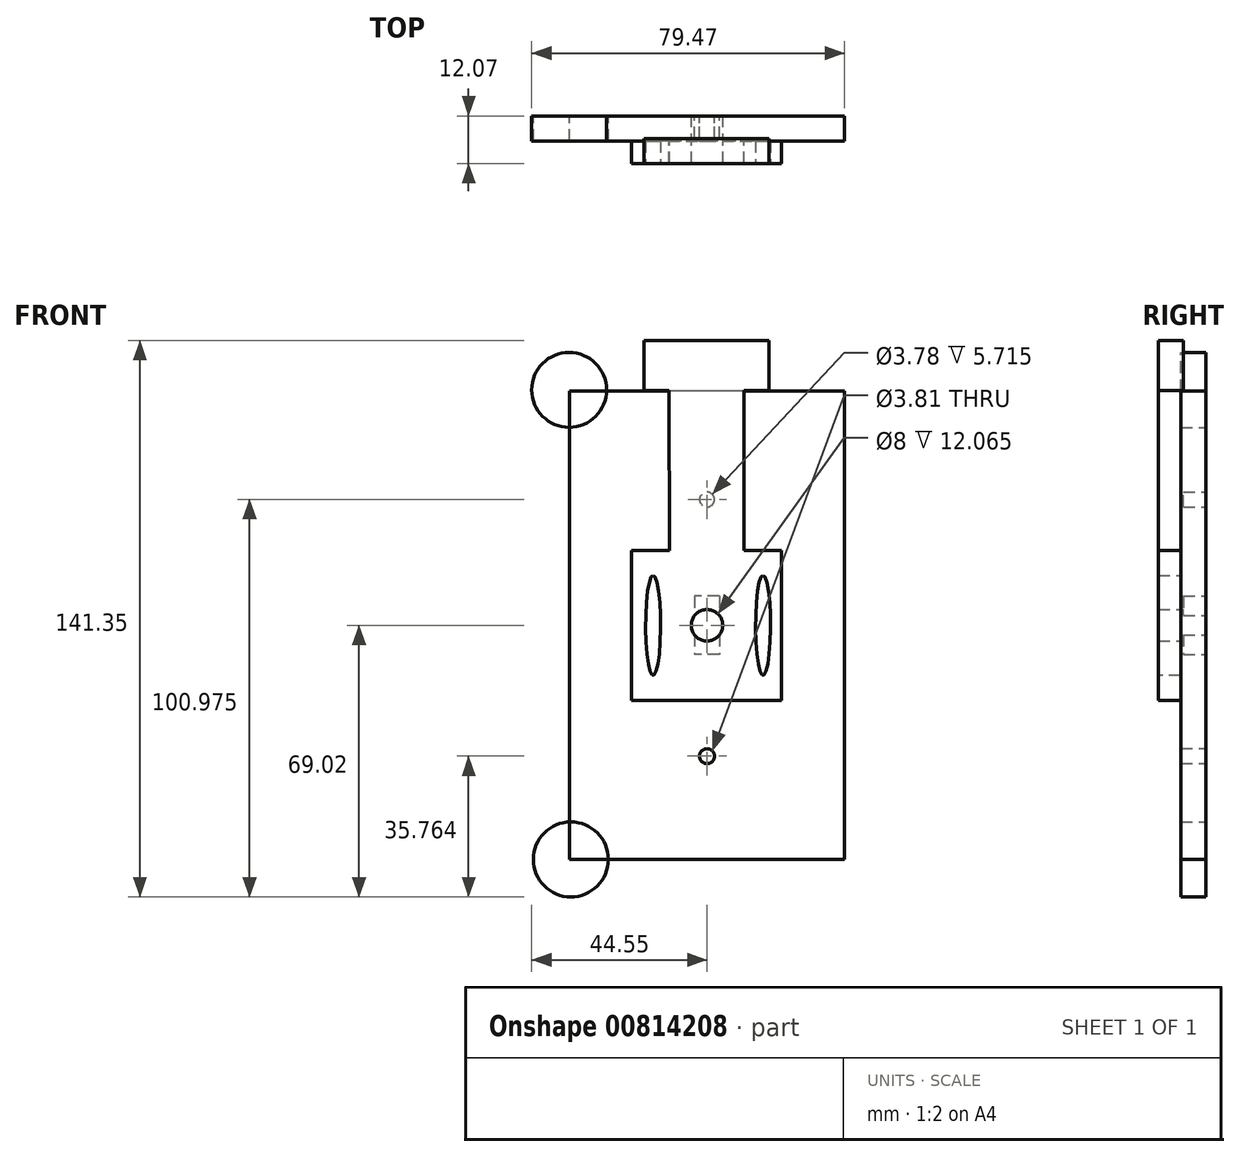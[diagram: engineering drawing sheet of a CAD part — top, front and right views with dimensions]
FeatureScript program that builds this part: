
annotation { "Feature Type Name" : "Feature", "Feature Type Description" : "" }
export const myFeature = defineFeature(function(context is Context, id is Id, definition is map)
    precondition{}
    {
        {
            var Q0;
            Q0=qCreatedBy(makeId("Front.planeOp"),FACE);
            var sketch = newSketch(context, id + "F0", { "sketchPlane" : qUnion([Q0])});
            skLineSegment(sketch, "E0.bottom", {"start": v(34.93, 59.53) * mm, "end": v(-34.93, 59.53) * mm});
            skLineSegment(sketch, "E0.top", {"start": v(34.92, -59.53) * mm, "end": v(-34.93, -59.53) * mm});
            skLineSegment(sketch, "E0.left", {"start": v(34.93, 59.53) * mm, "end": v(34.92, -59.53) * mm});
            skLineSegment(sketch, "E0.right", {"start": v(-34.93, 59.53) * mm, "end": v(-34.93, -59.53) * mm});
            skPoint(sketch, "E0.middle", {"position": v(0, 0) * mm});
            skLineSegment(sketch, "E1.bottom", {"start": v(3.18, 7.4) * mm, "end": v(-3.17, 7.4) * mm});
            skLineSegment(sketch, "E1.top", {"start": v(3.17, -7.4) * mm, "end": v(-3.18, -7.4) * mm});
            skLineSegment(sketch, "E1.left", {"start": v(3.18, 7.4) * mm, "end": v(3.17, -7.4) * mm});
            skLineSegment(sketch, "E1.right", {"start": v(-3.17, 7.4) * mm, "end": v(-3.18, -7.4) * mm});
            skCircle(sketch, "E2", {"center": v(0, 31.96) * mm, "radius": 1.9 * mm});
            skPoint(sketch, "E2.centerSnap0", {"position": v(0, 7.4) * mm});
            skCircle(sketch, "E3", {"center": v(0, -33.26) * mm, "radius": 1.9 * mm});
            skSolve(sketch);
        }
        {
            var Q0;
            Q0=qCreatedBy(makeId("Front.planeOp"),FACE);
            var sketch = newSketch(context, id + "F1", { "sketchPlane" : qUnion([Q0])});
            skCircle(sketch, "E4", {"center": v(-35.02, 59.81) * mm, "radius": 9.53 * mm});
            skSolve(sketch);
        }
        {
            var Q0;
            Q0=qCreatedBy(makeId("Front.planeOp"),FACE);
            var sketch = newSketch(context, id + "F2", { "sketchPlane" : qUnion([Q0])});
            skCircle(sketch, "E5", {"center": v(-34.6, -59.5) * mm, "radius": 9.53 * mm});
            skSolve(sketch);
        }
        {
            var Q0;
            Q0=makeQuery(id+"F2.imprint","IMPRINT",FACE,{"disambiguationData":[TD([[makeQuery(id+"F2.imprint","IMPRINT",EDGE,{"derivedFrom":sQuery(id+"F2.wireOp",EDGE,"E5")}),1.0]])]});
            var Q1;
            Q1=makeQuery(id+"F0.imprint","IMPRINT",FACE,{"disambiguationData":[TD([[makeQuery(id+"F0.imprint","IMPRINT",EDGE,{"derivedFrom":sQuery(id+"F0.wireOp",EDGE,"E0.bottom")}),1.0]])]});
            var Q2;
            Q2=makeQuery(id+"F1.imprint","IMPRINT",FACE,{"disambiguationData":[TD([[makeQuery(id+"F1.imprint","IMPRINT",EDGE,{"derivedFrom":sQuery(id+"F1.wireOp",EDGE,"E4")}),1.0]])]});
            extrude(context, id + "F3", {"entities" : qUnion([Q0, Q1, Q2]), "depth" : 6.35 * mm, "offsetDistance" : 25.4 * mm});
        }
        {
            var Q0;
            Q0=makeQuery(id+"FBm9dElFGxXl51s_0.boolean.opBoolean","MERGE",FACE,{"derivedFrom":[makeQuery(id+"F3.opExtrude","CAP_FACE",FACE,{"disambiguationData":[OSD([sQuery(id+"F0.wireOp",EDGE,"E0.bottom"),sQuery(id+"F0.wireOp",EDGE,"E0.top"),sQuery(id+"F0.wireOp",EDGE,"E0.left"),sQuery(id+"F0.wireOp",EDGE,"E0.right")])],"isStart":false}),makeQuery(id+"FBm9dElFGxXl51s_0.opExtrude","CAP_FACE",FACE,{"disambiguationData":[OSD([sQuery(id+"FwdLjQRzTwuGbji_0.wireOp",EDGE,"bJfUg37Y-0sjC-gCHG-03pR-bU85yGZvt3Yf.left"),sQuery(id+"FwdLjQRzTwuGbji_0.wireOp",EDGE,"bJfUg37Y-0sjC-gCHG-03pR-bU85yGZvt3Yf.right"),sQuery(id+"FwdLjQRzTwuGbji_0.wireOp",EDGE,"DSwXmp3Y-NZgs-XlkP-MrdE-YPkT81guO0ga"),sQuery(id+"FwdLjQRzTwuGbji_0.wireOp",EDGE,"yhkVxWKS-fieb-baY7-XOx3-TyVL69QeHBbo"),sQuery(id+"FwdLjQRzTwuGbji_0.wireOp",EDGE,"tSnspYBW-VqIu-ENpb-q0uR-903lSlMSbRlf"),sQuery(id+"FwdLjQRzTwuGbji_0.wireOp",EDGE,"O0cluCkd-JC2S-dvMv-2QXM-CzPiqj9PooOO"),sQuery(id+"FwdLjQRzTwuGbji_0.wireOp",EDGE,"txsKDkrA-VlTc-3cXs-rglu-60bT2i7TrSKH"),sQuery(id+"FwdLjQRzTwuGbji_0.wireOp",EDGE,"3i0H6R7e-R6fp-PJKQ-zfIY-D4jAGeBqw7su"),sQuery(id+"FwdLjQRzTwuGbji_0.wireOp",EDGE,"NDugy8ID-homc-AnxF-yfxB-C4huzXxJ8HOw"),sQuery(id+"FwdLjQRzTwuGbji_0.wireOp",EDGE,"kmT3zlDP-fOXE-ID7O-qQZw-wmLyp1ZqRsv8"),sQuery(id+"FwdLjQRzTwuGbji_0.wireOp",EDGE,"mg99yGsM-S2XL-aYIf-W8aI-fFjbHoOIm3QQ"),sQuery(id+"FwdLjQRzTwuGbji_0.wireOp",EDGE,"DyA1L4wi-5721-awLX-u9Y8-JtvzIZL4NBOm")])],"isStart":false})]});
            cPlane(context, id + "F4", {"entities" : qUnion([Q0]), "cplaneType" : CPlaneType.OFFSET, "offset" : 2.54 * mm, "width" : 152.4 * mm, "height" : 152.4 * mm});
        }
        {
            var Q0;
            Q0=qCreatedBy(id+"F4.planeOp",FACE);
            var sketch = newSketch(context, id + "F5", { "sketchPlane" : qUnion([Q0])});
            skLineSegment(sketch, "E6", {"start": v(-9.63, 59.63) * mm, "end": v(-15.99, 59.63) * mm});
            skLineSegment(sketch, "E7", {"start": v(-15.99, 59.63) * mm, "end": v(-15.99, 72.33) * mm});
            skLineSegment(sketch, "E8", {"start": v(-15.99, 72.33) * mm, "end": v(15.76, 72.33) * mm});
            skLineSegment(sketch, "E9", {"start": v(15.76, 72.33) * mm, "end": v(15.76, 59.63) * mm});
            skLineSegment(sketch, "E10", {"start": v(15.76, 59.63) * mm, "end": v(9.41, 59.63) * mm});
            skLineSegment(sketch, "E11", {"start": v(9.41, 59.63) * mm, "end": v(9.41, 18.99) * mm});
            skLineSegment(sketch, "E12", {"start": v(9.41, 18.99) * mm, "end": v(18.93, 18.99) * mm});
            skLineSegment(sketch, "E13", {"start": v(18.93, 18.99) * mm, "end": v(18.93, -19.11) * mm});
            skLineSegment(sketch, "E14", {"start": v(18.93, -19.11) * mm, "end": v(-19.17, -19.11) * mm});
            skLineSegment(sketch, "E15", {"start": v(-19.17, -19.11) * mm, "end": v(-19.17, 18.99) * mm});
            skLineSegment(sketch, "E16", {"start": v(-19.17, 18.99) * mm, "end": v(-9.5, 18.99) * mm});
            skLineSegment(sketch, "E17", {"start": v(-9.5, 18.99) * mm, "end": v(-9.63, 59.63) * mm});
            skEllipse(sketch, "E18", {"center": v(-13.68, 0) * mm, "majorRadius": 12.7 * mm, "minorRadius": 1.9 * mm, "majorAxis": v(0, 1)});
            skEllipse(sketch, "E19", {"center": v(14.25, 0) * mm, "majorRadius": 12.7 * mm, "minorRadius": 1.9 * mm, "majorAxis": v(0, 1)});
            skSolve(sketch);
        }
        {
            var Q0;
            Q0=makeQuery(id+"F5.imprint","IMPRINT",FACE,{"disambiguationData":[TD([[makeQuery(id+"F5.imprint","IMPRINT",EDGE,{"derivedFrom":sQuery(id+"F5.wireOp",EDGE,"E6")}),-1.0]])]});
            extrude(context, id + "F6", {"entities" : qUnion([Q0]), "operationType" : NewBodyOperationType.ADD, "endBound" : BoundingType.SYMMETRIC, "depth" : 6.35 * mm, "offsetDistance" : 25.4 * mm});
        }
        {
            var Q0;
            Q0=sQuery(id+"F0.wireOp",VERTEX,"E0.middle");
            var Q1;
            Q1=makeQuery(id+"F3.opExtrude","SWEPT_BODY",BODY,{"disambiguationData":[OSD([sQuery(id+"F0.wireOp",EDGE,"E0.bottom"),sQuery(id+"F0.wireOp",EDGE,"E0.top"),sQuery(id+"F0.wireOp",EDGE,"E0.left"),sQuery(id+"F0.wireOp",EDGE,"E0.right")])]});
            hole(context, id + "F7", {"style" : HoleStyle.SIMPLE, "endStyle" : HoleEndStyle.THROUGH, "oppositeDirection" : true, "holeDiameter" : 8 * mm, "majorDiameter" : 6.35 * mm, "isTappedThrough" : true, "tappedDepth" : 12.7 * mm, "tapClearance" : 3, "locations" : qUnion([Q0]), "scope" : qUnion([Q1])});
        }
    });
